# Revit family: SUPER LINEAL RGBW 100CM_LKA1220.22
name_source: partatom
category: Luminarias
units: mm (PartAtom-declared; Revit-internal decimal feet)

## family parameters
Compartido = No
Corte con vacíos al cargar = No
Cota de conector redondo = Diámetro de uso
Origen de luz = Sí
Punto de cálculo de habitación = No
Se basa en plano de trabajo = Sí
Siempre vertical = No
Tipo de pieza = Normal

## types (1)
- REFL_LKA1220.22
    Cambio de temperatura de color de luz atenuada = Curva de lámpara incandescente
    Comentarios de vataje = 24V
    Descripción = LUMINARIA TIPO REFLECTOR LINEAL, WALL WASHER , CUERPO DE ALUMINIO EXTRUIDO CON POLVO GRIS, VIDRIO TEMPLADO DE 3MM ADEMAS DEL SELLADO CON SILICON EN VIDRIO Y HOUSING, CUENTA CON 20 LED TIPO R=1000mA G=1000mA B=1000Ma W=1000mA  CON UN CONSUMO TOTAL DE 96W, 3523 LUMENES, RGBW, IP 65, IK 05, CABLE H05RN DE 0.5M, APERTURA EN STOCK DE 22 GRADOS, ALIMENTADA A 24V. REQUIERE ACCESORIOS.
    Elevación por defecto = 0 mm  [stored 0 ft]
    Fabricante = BRILLANT
    Filtro de color = 16777215
    Longitud de línea de emisión = 1000 mm  [stored 3.28084 ft]
    Longitud de símbolo de origen de luz = 500 mm  [stored 1.64042 ft]
    Lámpara = OSRAM
    Modelo = LKA1220.22
    Watt per fixture = 96
    Ángulo de campo de foco = 22.00°
    Ángulo de enfoque = 22.00°
    Ángulo de inclinación = 22.00°

note: [stored X ft] marks values corroborated as IEEE doubles in the binary element streams (Revit-internal decimal feet)

## geometry (parser evidence)
native form markers: Blend x2
no freeform markers — native parametric forms only
